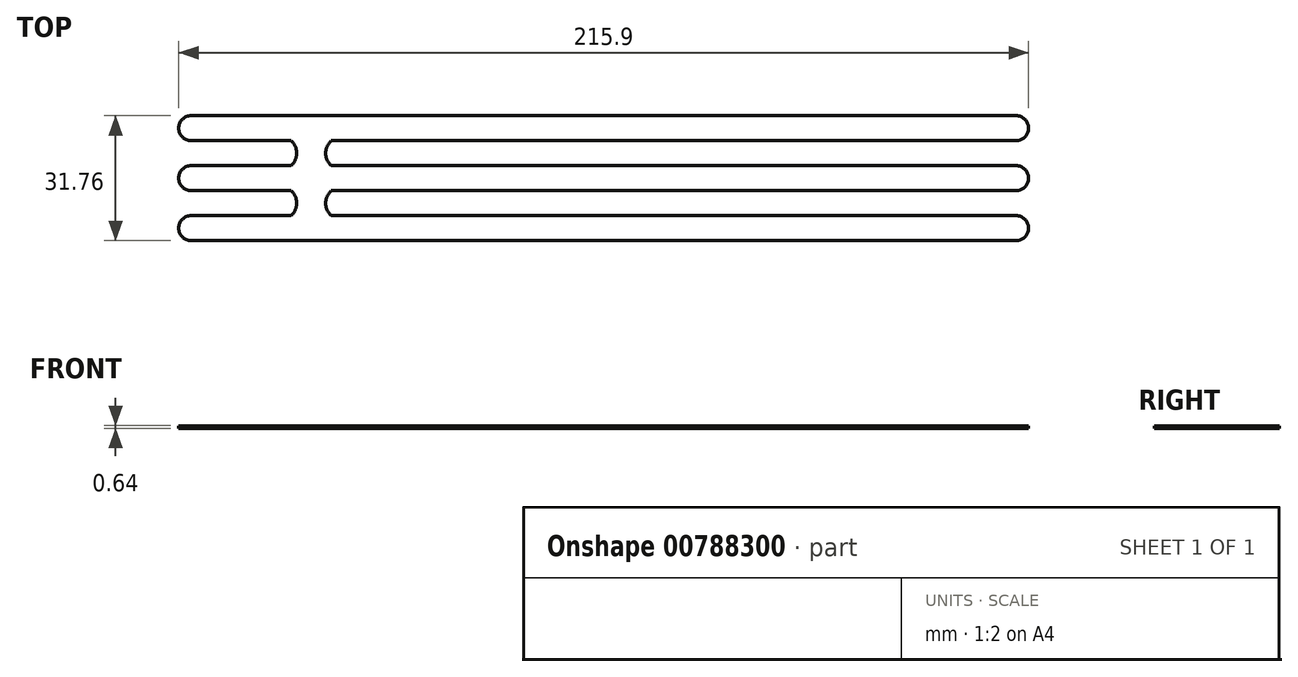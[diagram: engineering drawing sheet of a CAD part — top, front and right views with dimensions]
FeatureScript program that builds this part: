
annotation { "Feature Type Name" : "Feature", "Feature Type Description" : "" }
export const myFeature = defineFeature(function(context is Context, id is Id, definition is map)
    precondition{}
    {
        {
            var Q0;
            Q0=qCreatedBy(makeId("Top.planeOp"),FACE);
            var sketch = newSketch(context, id + "F0", { "sketchPlane" : qUnion([Q0])});
            skLineSegment(sketch, "E0.bottom", {"start": v(104.78, 3.17) * mm, "end": v(-104.78, 3.17) * mm});
            skLineSegment(sketch, "E0.top", {"start": v(104.78, -3.17) * mm, "end": v(-104.78, -3.17) * mm});
            skLineSegment(sketch, "E0.left", {"start": v(107.95, 0) * mm, "end": v(107.95, 0) * mm});
            skLineSegment(sketch, "E0.right", {"start": v(-107.95, 0) * mm, "end": v(-107.95, 0) * mm});
            skPoint(sketch, "E0.middle", {"position": v(0, 0) * mm});
            skPoint(sketch, "E1.visualSharp", {"position": v(-107.95, -3.17) * mm});
            skArc(sketch, "E1.filletArc", {"start": v(-107.95, 0) * mm, "mid": v(-107.02, -2.25) * mm, "end": v(-104.78, -3.17) * mm});
            skPoint(sketch, "E2.visualSharp", {"position": v(-107.95, 3.17) * mm});
            skArc(sketch, "E2.filletArc", {"start": v(-104.78, 3.17) * mm, "mid": v(-107.02, 2.25) * mm, "end": v(-107.95, 0) * mm});
            skPoint(sketch, "E3.visualSharp", {"position": v(107.95, 3.17) * mm});
            skArc(sketch, "E3.filletArc", {"start": v(107.95, 0) * mm, "mid": v(107.02, 2.25) * mm, "end": v(104.78, 3.17) * mm});
            skPoint(sketch, "E4.visualSharp", {"position": v(107.95, -3.17) * mm});
            skArc(sketch, "E4.filletArc", {"start": v(104.78, -3.17) * mm, "mid": v(107.02, -2.25) * mm, "end": v(107.95, 0) * mm});
            skLineSegment(sketch, "E5", {"start": v(0, 70.97) * mm, "end": v(0, -80.25) * mm, "construction": true});
            skLineSegment(sketch, "E6", {"start": v(-107.7, 6.35) * mm, "end": v(44.37, 6.35) * mm, "construction": true});
            skLineSegment(sketch, "E7.MirrorCS", {"start": v(0, -58.27) * mm, "end": v(0, 92.95) * mm, "construction": true});
            skLineSegment(sketch, "E8.MirrorCS", {"start": v(104.78, 9.52) * mm, "end": v(-104.78, 9.52) * mm});
            skArc(sketch, "E9.MirrorCS", {"start": v(-104.78, 9.52) * mm, "mid": v(-107.02, 10.45) * mm, "end": v(-107.95, 12.7) * mm});
            skArc(sketch, "E10.MirrorCS", {"start": v(-107.95, 12.7) * mm, "mid": v(-107.02, 14.95) * mm, "end": v(-104.78, 15.87) * mm});
            skLineSegment(sketch, "E11.MirrorCS", {"start": v(104.78, 15.87) * mm, "end": v(-104.78, 15.87) * mm});
            skPoint(sketch, "E12.MirrorP", {"position": v(107.95, 9.52) * mm});
            skArc(sketch, "E13.MirrorCS", {"start": v(107.95, 12.7) * mm, "mid": v(107.02, 10.45) * mm, "end": v(104.78, 9.52) * mm});
            skArc(sketch, "E14.MirrorCS", {"start": v(104.78, 15.87) * mm, "mid": v(107.02, 14.95) * mm, "end": v(107.95, 12.7) * mm});
            skLineSegment(sketch, "E15", {"start": v(-108.18, -6.35) * mm, "end": v(44.34, -6.35) * mm, "construction": true});
            skLineSegment(sketch, "E16.MirrorCS", {"start": v(104.78, -9.53) * mm, "end": v(-104.78, -9.53) * mm});
            skArc(sketch, "E17.MirrorCS", {"start": v(-107.95, -12.7) * mm, "mid": v(-107.02, -10.45) * mm, "end": v(-104.78, -9.52) * mm});
            skArc(sketch, "E18.MirrorCS", {"start": v(-104.78, -15.87) * mm, "mid": v(-107.02, -14.95) * mm, "end": v(-107.95, -12.7) * mm});
            skLineSegment(sketch, "E19.MirrorCS", {"start": v(104.78, -15.88) * mm, "end": v(-104.78, -15.88) * mm});
            skArc(sketch, "E20.MirrorCS", {"start": v(107.95, -12.7) * mm, "mid": v(107.02, -14.95) * mm, "end": v(104.78, -15.87) * mm});
            skArc(sketch, "E21.MirrorCS", {"start": v(104.78, -9.52) * mm, "mid": v(107.02, -10.45) * mm, "end": v(107.95, -12.7) * mm});
            skLineSegment(sketch, "E22", {"start": v(-74.3, 29) * mm, "end": v(-74.3, -32.24) * mm});
            skLineSegment(sketch, "E23", {"start": v(0, 0) * mm, "end": v(-90.15, 0) * mm, "construction": true});
            skArc(sketch, "E24", {"start": v(-79.37, -9.53) * mm, "mid": v(-77.98, -6.35) * mm, "end": v(-79.38, -3.17) * mm});
            skArc(sketch, "E25", {"start": v(-69.22, -3.17) * mm, "mid": v(-70.6, -6.35) * mm, "end": v(-69.22, -9.53) * mm});
            skArc(sketch, "E26", {"start": v(-79.38, 3.17) * mm, "mid": v(-77.98, 6.35) * mm, "end": v(-79.38, 9.52) * mm});
            skArc(sketch, "E27", {"start": v(-69.22, 9.52) * mm, "mid": v(-70.6, 6.35) * mm, "end": v(-69.22, 3.17) * mm});
            skPoint(sketch, "E28.center.orphan", {"position": v(-79.38, 6.35) * mm});
            skSolve(sketch);
        }
        {
            var Q0;
            Q0=makeQuery(id+"F0.imprint","IMPRINT",FACE,{"disambiguationData":[TD([[makeQuery(id+"F0.imprint","IMPRINT",EDGE,{"derivedFrom":sQuery(id+"F0.wireOp",EDGE,"E0.bottom")}),1.0]])]});
            var Q1;
            {var subQ4=sQuery(id+"F0.wireOp",EDGE,"E8.MirrorCS");Q1=makeQuery(id+"F0.imprint","IMPRINT",FACE,{"disambiguationData":[TD([[makeQuery(id+"F0.imprint","IMPRINT",EDGE,{"derivedFrom":subQ4}),-1.0]])]});}
            var Q2;
            {var subQ4=sQuery(id+"F0.wireOp",EDGE,"E16.MirrorCS");Q2=makeQuery(id+"F0.imprint","IMPRINT",FACE,{"disambiguationData":[TD([[makeQuery(id+"F0.imprint","IMPRINT",EDGE,{"derivedFrom":subQ4}),1.0]])]});}
            var Q3;
            {var subQ0=sQuery(id+"F0.wireOp",EDGE,"E28");Q3=makeQuery(id+"F0.imprint","IMPRINT",FACE,{"disambiguationData":[TD([[makeQuery(id+"F0.imprint","IMPRINT",EDGE,{"derivedFrom":subQ0}),-1.0]])]});}
            var Q4;
            {var subQ0=sQuery(id+"F0.wireOp",EDGE,"a1320bb3-af1a-47d3-bc95-bfbaaebf015f0.MirrorC");Q4=makeQuery(id+"F0.imprint","IMPRINT",FACE,{"disambiguationData":[TD([[makeQuery(id+"F0.imprint","IMPRINT",EDGE,{"derivedFrom":subQ0}),1.0]])]});}
            var Q5;
            {var subQ0=sQuery(id+"F0.wireOp",EDGE,"c81fd363-d494-4e79-9f9a-4ea18c2d69c70.MirrorC");Q5=makeQuery(id+"F0.imprint","IMPRINT",FACE,{"disambiguationData":[TD([[makeQuery(id+"F0.imprint","IMPRINT",EDGE,{"derivedFrom":subQ0}),1.0]])]});}
            var Q6;
            {var subQ0=sQuery(id+"F0.wireOp",EDGE,"288a92cd-7641-47cf-aff3-7e6178ed43660.MirrorC");Q6=makeQuery(id+"F0.imprint","IMPRINT",FACE,{"disambiguationData":[TD([[makeQuery(id+"F0.imprint","IMPRINT",EDGE,{"derivedFrom":subQ0}),-1.0]])]});}
            var Q7;
            {var subQ0=sQuery(id+"F0.wireOp",EDGE,"E26");Q7=makeQuery(id+"F0.imprint","IMPRINT",FACE,{"disambiguationData":[TD([[makeQuery(id+"F0.imprint","IMPRINT",EDGE,{"derivedFrom":subQ0}),-1.0]])]});}
            var Q8;
            {var subQ0=sQuery(id+"F0.wireOp",EDGE,"E27");Q8=makeQuery(id+"F0.imprint","IMPRINT",FACE,{"disambiguationData":[TD([[makeQuery(id+"F0.imprint","IMPRINT",EDGE,{"derivedFrom":subQ0}),-1.0]])]});}
            var Q9;
            {var subQ0=sQuery(id+"F0.wireOp",EDGE,"E24");Q9=makeQuery(id+"F0.imprint","IMPRINT",FACE,{"disambiguationData":[TD([[makeQuery(id+"F0.imprint","IMPRINT",EDGE,{"derivedFrom":subQ0}),-1.0]])]});}
            var Q10;
            {var subQ0=sQuery(id+"F0.wireOp",EDGE,"E25");Q10=makeQuery(id+"F0.imprint","IMPRINT",FACE,{"disambiguationData":[TD([[makeQuery(id+"F0.imprint","IMPRINT",EDGE,{"derivedFrom":subQ0}),-1.0]])]});}
            extrude(context, id + "F1", {"entities" : qUnion([Q0, Q1, Q2, Q3, Q4, Q5, Q6, Q7, Q8, Q9, Q10]), "depth" : 0.64 * mm, "offsetDistance" : 25.4 * mm});
        }
    });
